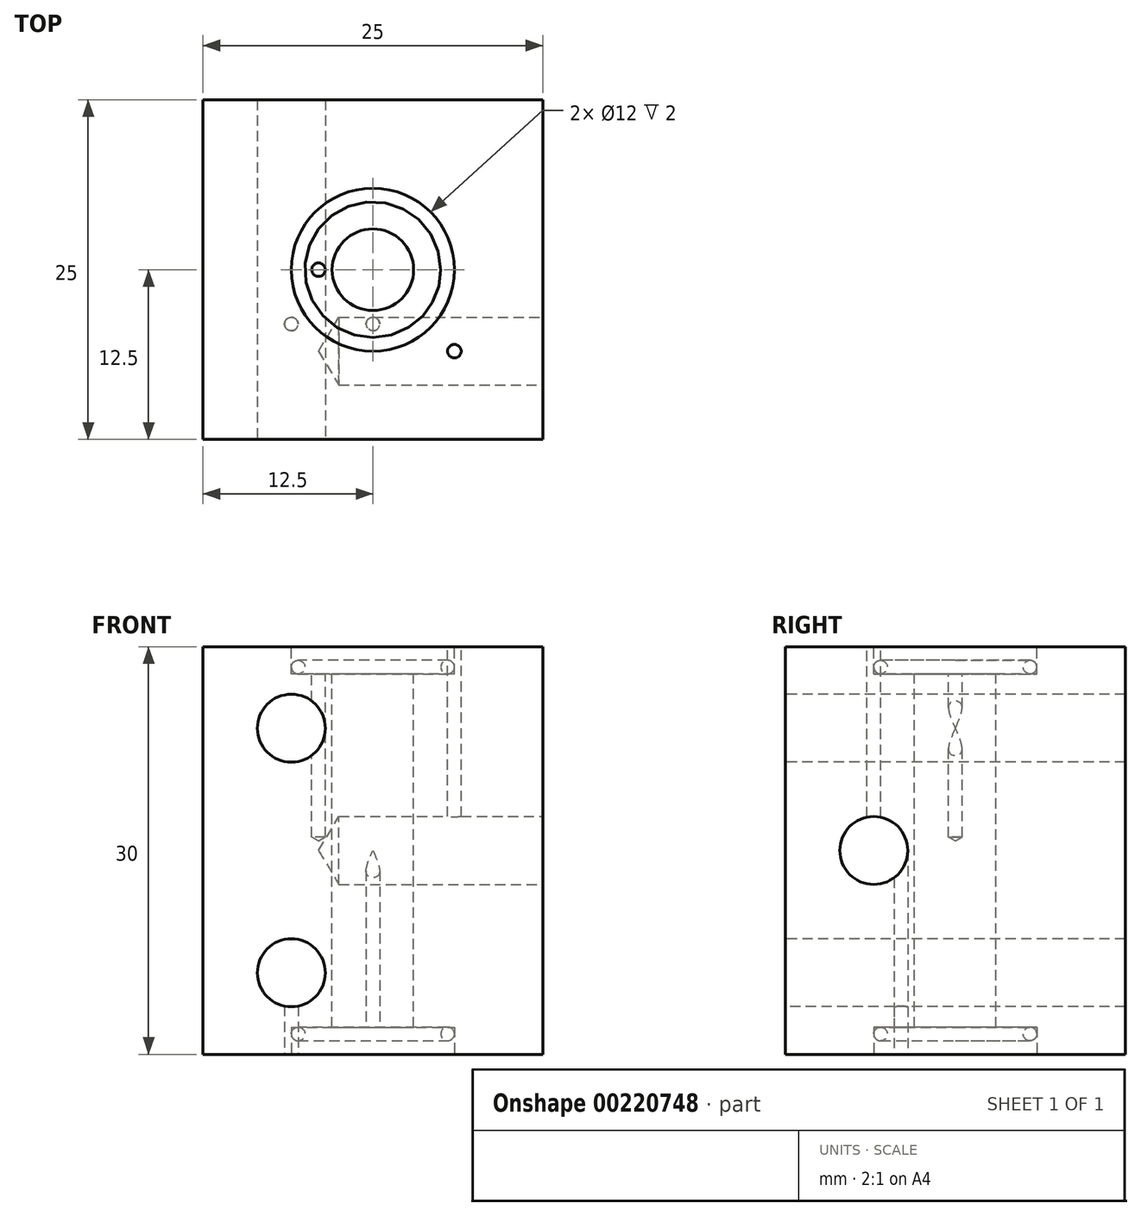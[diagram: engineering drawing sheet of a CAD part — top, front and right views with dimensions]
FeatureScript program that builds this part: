
annotation { "Feature Type Name" : "Feature", "Feature Type Description" : "" }
export const myFeature = defineFeature(function(context is Context, id is Id, definition is map)
    precondition{}
    {
        {
            var Q0;
            Q0=qCreatedBy(makeId("Front.planeOp"),FACE);
            var sketch = newSketch(context, id + "F0", { "sketchPlane" : qUnion([Q0])});
            skLineSegment(sketch, "E0.bottom", {"start": v(0, 0) * mm, "end": v(25, 0) * mm});
            skLineSegment(sketch, "E0.top", {"start": v(0, 30) * mm, "end": v(25, 30) * mm});
            skLineSegment(sketch, "E0.left", {"start": v(0, 0) * mm, "end": v(0, 30) * mm});
            skLineSegment(sketch, "E0.right", {"start": v(25, 0) * mm, "end": v(25, 30) * mm});
            skSolve(sketch);
        }
        {
            var Q0;
            Q0=qSketchRegion(id+"F0",true);
            extrude(context, id + "F1", {"entities" : qUnion([Q0]), "endBound" : BoundingType.SYMMETRIC, "depth" : 25 * mm});
        }
        {
            var Q0;
            Q0=makeQuery(id+"F1.opExtrude","SWEPT_FACE",FACE,{"disambiguationData":[OSD([sQuery(id+"F0.wireOp",EDGE,"E0.top")])]});
            var sketch = newSketch(context, id + "F2", { "sketchPlane" : qUnion([Q0])});
            skLineSegment(sketch, "E1.0", {"start": v(0, 0) * mm, "end": v(25, 0) * mm, "construction": true});
            skPoint(sketch, "E2", {"position": v(12.5, 0) * mm});
            skPoint(sketch, "E3", {"position": v(8.5, 0) * mm});
            skLineSegment(sketch, "E4", {"start": v(0, -6) * mm, "end": v(25, -6) * mm, "construction": true});
            skPoint(sketch, "E5", {"position": v(12.5, -6) * mm});
            skPoint(sketch, "E6", {"position": v(18.5, -6) * mm});
            skSolve(sketch);
        }
        {
            var Q0;
            Q0=sQuery(id+"F2.wireOp",VERTEX,"E2");
            var Q1;
            Q1=makeQuery(id+"F1.opExtrude","SWEPT_BODY",BODY,{"disambiguationData":[OSD([sQuery(id+"F0.wireOp",EDGE,"E0.bottom"),sQuery(id+"F0.wireOp",EDGE,"E0.top"),sQuery(id+"F0.wireOp",EDGE,"E0.left"),sQuery(id+"F0.wireOp",EDGE,"E0.right")])]});
            hole(context, id + "F12", {"style" : HoleStyle.C_BORE, "endStyle" : HoleEndStyle.THROUGH, "standardTappedOrClearance" : lookupTablePath({ "standard" : "ISO", "type" : "Drilled" }), "standardBlindInLast" : lookupTablePath({ "standard" : "ISO", "type" : "Drilled" }), "holeDiameter" : 6 * mm, "cBoreDiameter" : 12 * mm, "cBoreDepth" : 2 * mm, "locations" : qUnion([Q0]), "scope" : qUnion([Q1]), "isTappedThrough" : true});
        }
        {
            var Q0;
            Q0=makeQuery(id+"F1.opExtrude","CAP_FACE",FACE,{"disambiguationData":[OSD([sQuery(id+"F0.wireOp",EDGE,"E0.bottom"),sQuery(id+"F0.wireOp",EDGE,"E0.top"),sQuery(id+"F0.wireOp",EDGE,"E0.left"),sQuery(id+"F0.wireOp",EDGE,"E0.right")])],"isStart":false});
            var sketch = newSketch(context, id + "F13", { "sketchPlane" : qUnion([Q0])});
            skLineSegment(sketch, "E7.0", {"start": v(0, 30) * mm, "end": v(25, 30) * mm, "construction": true});
            skLineSegment(sketch, "E8.0", {"start": v(0, 0) * mm, "end": v(25, 0) * mm, "construction": true});
            skLineSegment(sketch, "E9", {"start": v(12.5, 30) * mm, "end": v(12.5, 0) * mm, "construction": true});
            skLineSegment(sketch, "E10", {"start": v(6.5, 30) * mm, "end": v(6.5, 0) * mm, "construction": true});
            skLineSegment(sketch, "E11", {"start": v(25, 30) * mm, "end": v(25, 0) * mm, "construction": true});
            skLineSegment(sketch, "E12", {"start": v(0, 30) * mm, "end": v(0, 0) * mm, "construction": true});
            skLineSegment(sketch, "E13", {"start": v(0, 6) * mm, "end": v(25, 6) * mm, "construction": true});
            skPoint(sketch, "E14", {"position": v(6.5, 6) * mm});
            skLineSegment(sketch, "E15", {"start": v(0, 24) * mm, "end": v(25, 24) * mm, "construction": true});
            skPoint(sketch, "E16", {"position": v(6.5, 24) * mm});
            skSolve(sketch);
        }
        {
            var Q0;
            Q0=sQuery(id+"F13.wireOp",VERTEX,"E14");
            var Q1;
            Q1=makeQuery(id+"F1.opExtrude","SWEPT_BODY",BODY,{"disambiguationData":[OSD([sQuery(id+"F0.wireOp",EDGE,"E0.bottom"),sQuery(id+"F0.wireOp",EDGE,"E0.top"),sQuery(id+"F0.wireOp",EDGE,"E0.left"),sQuery(id+"F0.wireOp",EDGE,"E0.right")])]});
            hole(context, id + "F3", {"style" : HoleStyle.SIMPLE, "endStyle" : HoleEndStyle.THROUGH, "standardTappedOrClearance" : lookupTablePath({ "standard" : "ISO" }), "standardBlindInLast" : lookupTablePath({ "standard" : "ISO" }), "holeDiameter" : 5 * mm, "locations" : qUnion([Q0]), "scope" : qUnion([Q1]), "isTappedThrough" : true});
        }
        {
            var Q0;
            Q0=sQuery(id+"F13.wireOp",VERTEX,"E16");
            var Q1;
            Q1=makeQuery(id+"F1.opExtrude","SWEPT_BODY",BODY,{"disambiguationData":[OSD([sQuery(id+"F0.wireOp",EDGE,"E0.bottom"),sQuery(id+"F0.wireOp",EDGE,"E0.top"),sQuery(id+"F0.wireOp",EDGE,"E0.left"),sQuery(id+"F0.wireOp",EDGE,"E0.right")])]});
            hole(context, id + "F14", {"style" : HoleStyle.SIMPLE, "endStyle" : HoleEndStyle.THROUGH, "standardTappedOrClearance" : lookupTablePath({ "standard" : "ISO" }), "standardBlindInLast" : lookupTablePath({ "standard" : "ISO" }), "holeDiameter" : 5 * mm, "locations" : qUnion([Q0]), "scope" : qUnion([Q1]), "isTappedThrough" : true});
        }
        {
            var Q0;
            Q0=makeQuery(id+"F1.opExtrude","SWEPT_FACE",FACE,{"disambiguationData":[OSD([sQuery(id+"F0.wireOp",EDGE,"E0.right")])]});
            var sketch = newSketch(context, id + "F4", { "sketchPlane" : qUnion([Q0])});
            skLineSegment(sketch, "E17.0", {"start": v(-12.5, 30) * mm, "end": v(12.5, 30) * mm, "construction": true});
            skLineSegment(sketch, "E18.0", {"start": v(0, 0) * mm, "end": v(0, 30) * mm, "construction": true});
            skLineSegment(sketch, "E19.0", {"start": v(-12.5, 0) * mm, "end": v(12.5, 0) * mm, "construction": true});
            skLineSegment(sketch, "E20.0", {"start": v(-12.5, 0) * mm, "end": v(-12.5, 30) * mm, "construction": true});
            skLineSegment(sketch, "E21", {"start": v(-6, 30) * mm, "end": v(-6, 0) * mm, "construction": true});
            skPoint(sketch, "E22", {"position": v(-6, 15) * mm});
            skSolve(sketch);
        }
        {
            var Q0;
            Q0=sQuery(id+"F4.wireOp",VERTEX,"E22");
            var Q1;
            Q1=makeQuery(id+"F1.opExtrude","SWEPT_BODY",BODY,{"disambiguationData":[OSD([sQuery(id+"F0.wireOp",EDGE,"E0.bottom"),sQuery(id+"F0.wireOp",EDGE,"E0.top"),sQuery(id+"F0.wireOp",EDGE,"E0.left"),sQuery(id+"F0.wireOp",EDGE,"E0.right")])]});
            hole(context, id + "F5", {"style" : HoleStyle.SIMPLE, "endStyle" : HoleEndStyle.BLIND, "standardTappedOrClearance" : lookupTablePath({ "standard" : "ISO" }), "standardBlindInLast" : lookupTablePath({ "standard" : "ISO" }), "holeDiameter" : 5 * mm, "holeDepth" : 15 * mm, "locations" : qUnion([Q0]), "scope" : qUnion([Q1])});
        }
        {
            var Q0;
            Q0=sQuery(id+"F2.wireOp",VERTEX,"E3");
            var Q1;
            Q1=makeQuery(id+"F1.opExtrude","SWEPT_BODY",BODY,{"disambiguationData":[OSD([sQuery(id+"F0.wireOp",EDGE,"E0.bottom"),sQuery(id+"F0.wireOp",EDGE,"E0.top"),sQuery(id+"F0.wireOp",EDGE,"E0.left"),sQuery(id+"F0.wireOp",EDGE,"E0.right")])]});
            hole(context, id + "F6", {"style" : HoleStyle.SIMPLE, "endStyle" : HoleEndStyle.BLIND, "standardTappedOrClearance" : lookupTablePath({ "standard" : "ISO", "size" : "1", "type" : "Drilled" }), "standardBlindInLast" : lookupTablePath({ "standard" : "ISO", "size" : "1", "type" : "Drilled" }), "holeDiameter" : 1 * mm, "holeDepth" : 12 * mm, "locations" : qUnion([Q0]), "scope" : qUnion([Q1])});
        }
        {
            var Q0;
            Q0=sQuery(id+"F2.wireOp",VERTEX,"E6");
            var Q1;
            Q1=makeQuery(id+"F1.opExtrude","SWEPT_BODY",BODY,{"disambiguationData":[OSD([sQuery(id+"F0.wireOp",EDGE,"E0.bottom"),sQuery(id+"F0.wireOp",EDGE,"E0.top"),sQuery(id+"F0.wireOp",EDGE,"E0.left"),sQuery(id+"F0.wireOp",EDGE,"E0.right")])]});
            hole(context, id + "F15", {"style" : HoleStyle.SIMPLE, "endStyle" : HoleEndStyle.BLIND, "standardTappedOrClearance" : lookupTablePath({ "standard" : "ISO", "size" : "1", "type" : "Drilled" }), "standardBlindInLast" : lookupTablePath({ "standard" : "ISO", "size" : "1", "type" : "Drilled" }), "holeDiameter" : 1 * mm, "holeDepth" : 15 * mm, "locations" : qUnion([Q0]), "scope" : qUnion([Q1])});
        }
        {
            var Q0;
            Q0=qCreatedBy(makeId("Top.planeOp"),FACE);
            var sketch = newSketch(context, id + "F7", { "sketchPlane" : qUnion([Q0])});
            skPoint(sketch, "E23.0", {"position": v(12.5, 0) * mm});
            skLineSegment(sketch, "E24.0.0", {"start": v(25, 12.5) * mm, "end": v(0, 12.5) * mm});
            skLineSegment(sketch, "E24.0.1", {"start": v(0, 12.5) * mm, "end": v(0, -12.5) * mm});
            skLineSegment(sketch, "E24.0.2", {"start": v(0, -12.5) * mm, "end": v(25, -12.5) * mm});
            skLineSegment(sketch, "E24.0.3", {"start": v(25, -12.5) * mm, "end": v(25, 12.5) * mm});
            skLineSegment(sketch, "E25.0", {"start": v(0, 0) * mm, "end": v(25, 0) * mm, "construction": true});
            skLineSegment(sketch, "E26", {"start": v(0, -4) * mm, "end": v(25, -4) * mm, "construction": true});
            skPoint(sketch, "E27", {"position": v(12.5, -4) * mm});
            skPoint(sketch, "E28", {"position": v(6.5, -4) * mm});
            skSolve(sketch);
        }
        {
            var Q0;
            Q0=sQuery(id+"F7.wireOp",VERTEX,"E27");
            var Q1;
            Q1=makeQuery(id+"F1.opExtrude","SWEPT_BODY",BODY,{"disambiguationData":[OSD([sQuery(id+"F0.wireOp",EDGE,"E0.bottom"),sQuery(id+"F0.wireOp",EDGE,"E0.top"),sQuery(id+"F0.wireOp",EDGE,"E0.left"),sQuery(id+"F0.wireOp",EDGE,"E0.right")])]});
            hole(context, id + "F16", {"style" : HoleStyle.SIMPLE, "endStyle" : HoleEndStyle.BLIND, "oppositeDirection" : true, "standardTappedOrClearance" : lookupTablePath({ "standard" : "ISO", "size" : "1", "type" : "Drilled" }), "standardBlindInLast" : lookupTablePath({ "standard" : "ISO", "size" : "1", "type" : "Drilled" }), "holeDiameter" : 1 * mm, "holeDepth" : 15 * mm, "locations" : qUnion([Q0]), "scope" : qUnion([Q1])});
        }
        {
            var Q0;
            Q0=sQuery(id+"F7.wireOp",VERTEX,"E28");
            var Q1;
            Q1=makeQuery(id+"F1.opExtrude","SWEPT_BODY",BODY,{"disambiguationData":[OSD([sQuery(id+"F0.wireOp",EDGE,"E0.bottom"),sQuery(id+"F0.wireOp",EDGE,"E0.top"),sQuery(id+"F0.wireOp",EDGE,"E0.left"),sQuery(id+"F0.wireOp",EDGE,"E0.right")])]});
            hole(context, id + "F8", {"style" : HoleStyle.SIMPLE, "endStyle" : HoleEndStyle.BLIND, "oppositeDirection" : true, "standardTappedOrClearance" : lookupTablePath({ "standard" : "ISO", "size" : "1", "type" : "Drilled" }), "standardBlindInLast" : lookupTablePath({ "standard" : "ISO", "size" : "1", "type" : "Drilled" }), "holeDiameter" : 1 * mm, "holeDepth" : 8 * mm, "locations" : qUnion([Q0]), "scope" : qUnion([Q1])});
        }
        {
            var Q0;
            Q0=sQuery(id+"F7.wireOp",VERTEX,"E23.0");
            var Q1;
            Q1=makeQuery(id+"F1.opExtrude","SWEPT_BODY",BODY,{"disambiguationData":[OSD([sQuery(id+"F0.wireOp",EDGE,"E0.bottom"),sQuery(id+"F0.wireOp",EDGE,"E0.top"),sQuery(id+"F0.wireOp",EDGE,"E0.left"),sQuery(id+"F0.wireOp",EDGE,"E0.right")])]});
            hole(context, id + "F9", {"style" : HoleStyle.C_BORE, "endStyle" : HoleEndStyle.BLIND, "oppositeDirection" : true, "standardTappedOrClearance" : lookupTablePath({ "standard" : "ISO", "size" : "6", "type" : "Drilled" }), "standardBlindInLast" : lookupTablePath({ "standard" : "ISO", "size" : "6", "type" : "Drilled" }), "holeDiameter" : 6 * mm, "cBoreDiameter" : 12 * mm, "cBoreDepth" : 2 * mm, "holeDepth" : 2 * mm, "startFromSketch" : true, "locations" : qUnion([Q0]), "scope" : qUnion([Q1])});
        }
        {
            var Q0;
            Q0=qCreatedBy(makeId("Front.planeOp"),FACE);
            var sketch = newSketch(context, id + "F17", { "sketchPlane" : qUnion([Q0])});
            skLineSegment(sketch, "E29", {"start": v(6.5, 0) * mm, "end": v(6.5, 1.5) * mm, "construction": true});
            skLineSegment(sketch, "E30", {"start": v(18.5, 2) * mm, "end": v(18.5, 0) * mm, "construction": true});
            skLineSegment(sketch, "E31.0.0", {"start": v(18.5, 2) * mm, "end": v(7, 2) * mm, "construction": true});
            skLineSegment(sketch, "E32", {"start": v(18.5, 30) * mm, "end": v(18.5, 28) * mm, "construction": true});
            skLineSegment(sketch, "E33", {"start": v(6.5, 28.5) * mm, "end": v(6.5, 30) * mm, "construction": true});
            skLineSegment(sketch, "E34.0.0", {"start": v(7, 28) * mm, "end": v(18.5, 28) * mm, "construction": true});
            skLineSegment(sketch, "E35.0.0", {"start": v(25, 30) * mm, "end": v(0, 30) * mm, "construction": true});
            skLineSegment(sketch, "E35.0.2", {"start": v(0, 30) * mm, "end": v(25, 30) * mm, "construction": true});
            skLineSegment(sketch, "E36.0.0", {"start": v(0, 0) * mm, "end": v(25, 0) * mm, "construction": true});
            skLineSegment(sketch, "E36.0.2", {"start": v(25, 0) * mm, "end": v(0, 0) * mm, "construction": true});
            skLineSegment(sketch, "E37", {"start": v(12.5, 30) * mm, "end": v(12.5, 0) * mm, "construction": true});
            skPoint(sketch, "E38.visualSharp", {"position": v(6.5, 28) * mm});
            skArc(sketch, "E38.filletArc", {"start": v(6.5, 28.5) * mm, "mid": v(6.65, 28.15) * mm, "end": v(7, 28) * mm, "construction": true});
            skPoint(sketch, "E39.visualSharp", {"position": v(6.5, 2) * mm});
            skArc(sketch, "E39.filletArc", {"start": v(7, 2) * mm, "mid": v(6.65, 1.85) * mm, "end": v(6.5, 1.5) * mm, "construction": true});
            skCircle(sketch, "E40", {"center": v(7, 1.5) * mm, "radius": 0.5 * mm});
            skCircle(sketch, "E41", {"center": v(7, 28.5) * mm, "radius": 0.5 * mm});
            skSolve(sketch);
        }
        {
            var Q0;
            Q0=makeQuery(id+"F17.imprint","IMPRINT",FACE,{"disambiguationData":[TD([[makeQuery(id+"F17.imprint","IMPRINT",EDGE,{"derivedFrom":sQuery(id+"F17.wireOp",EDGE,"E41")}),1.0]])]});
            var Q1;
            Q1=sQuery(id+"F17.wireOp",EDGE,"E37");
            revolve(context, id + "F10", {"entities" : qUnion([Q0]), "axis" : qUnion([Q1]), "revolveType" : RevolveType.FULL});
        }
        {
            var Q0;
            Q0=makeQuery(id+"F17.imprint","IMPRINT",FACE,{"disambiguationData":[TD([[makeQuery(id+"F17.imprint","IMPRINT",EDGE,{"derivedFrom":sQuery(id+"F17.wireOp",EDGE,"E40")}),1.0]])]});
            var Q1;
            Q1=sQuery(id+"F17.wireOp",EDGE,"E37");
            revolve(context, id + "F11", {"entities" : qUnion([Q0]), "axis" : qUnion([Q1]), "revolveType" : RevolveType.FULL});
        }
    });
